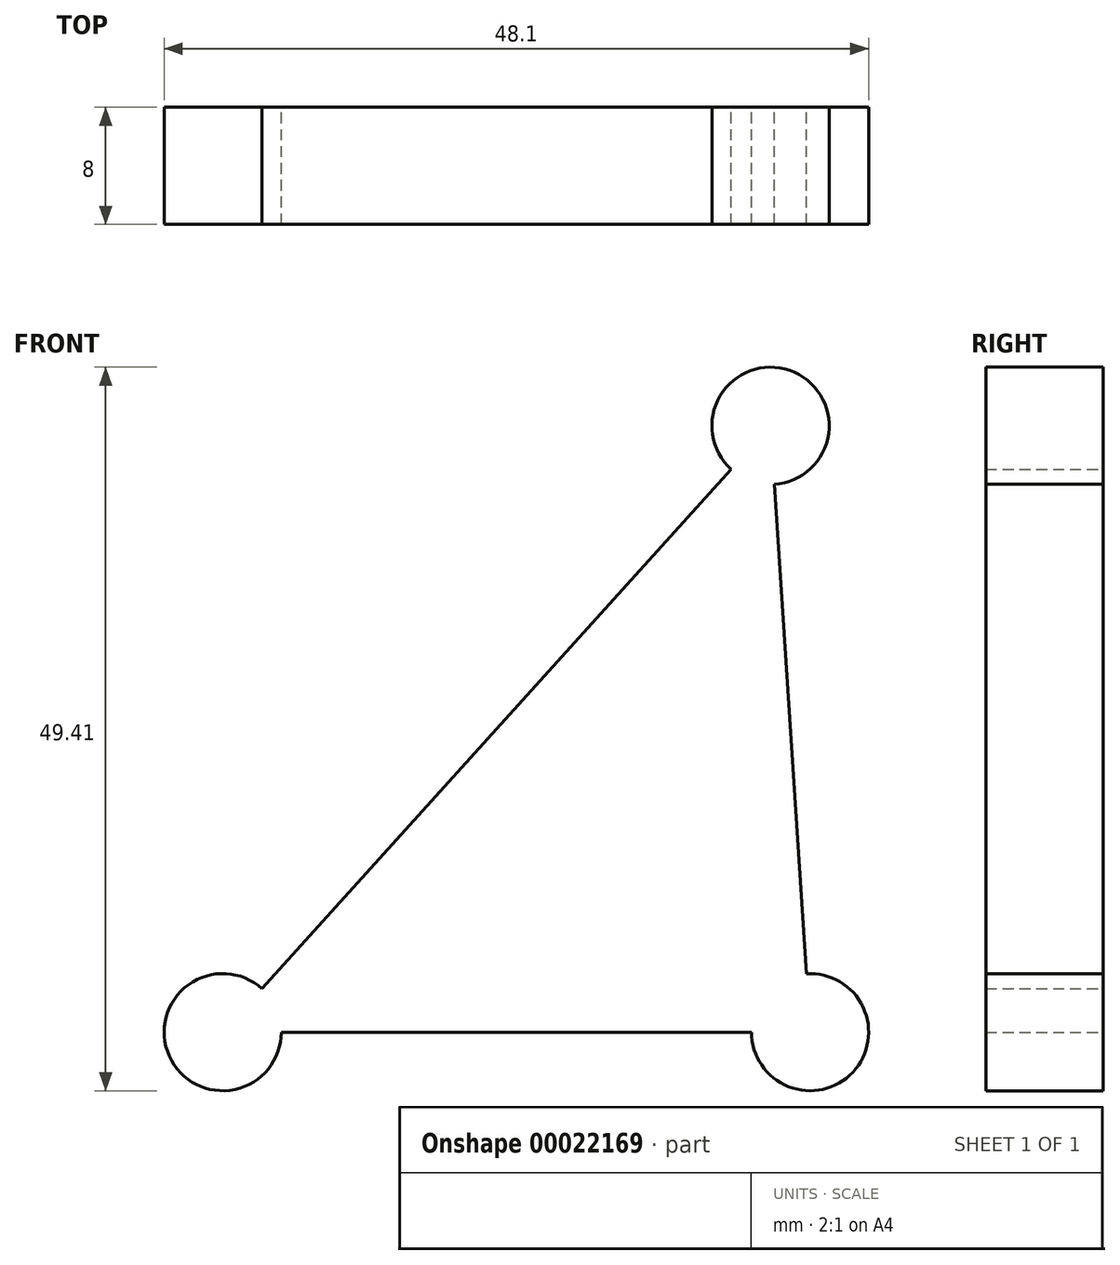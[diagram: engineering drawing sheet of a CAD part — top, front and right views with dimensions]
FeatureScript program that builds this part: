
annotation { "Feature Type Name" : "Feature", "Feature Type Description" : "" }
export const myFeature = defineFeature(function(context is Context, id is Id, definition is map)
    precondition{}
    {
        {
            var Q0;
            Q0=qCreatedBy(makeId("Front.planeOp"),FACE);
            var sketch = newSketch(context, id + "F0", { "sketchPlane" : qUnion([Q0])});
            skLineSegment(sketch, "E0", {"start": v(0, 0) * mm, "end": v(40.1, 0) * mm});
            skLineSegment(sketch, "E1", {"start": v(40.1, 0) * mm, "end": v(37.4, 41.41) * mm});
            skLineSegment(sketch, "E2", {"start": v(37.4, 41.41) * mm, "end": v(0, 0) * mm});
            skCircle(sketch, "E3", {"center": v(37.4, 41.41) * mm, "radius": 4 * mm});
            skCircle(sketch, "E4", {"center": v(40.1, 0) * mm, "radius": 4 * mm});
            skCircle(sketch, "E5", {"center": v(0, 0) * mm, "radius": 4 * mm});
            skSolve(sketch);
        }
        {
            var Q0;
            Q0 = qSketchRegion(id + "F0", true);
            extrude(context, id + "F1", {"entities" : qUnion([Q0]), "depth" : 8 * mm});
        }
    });
